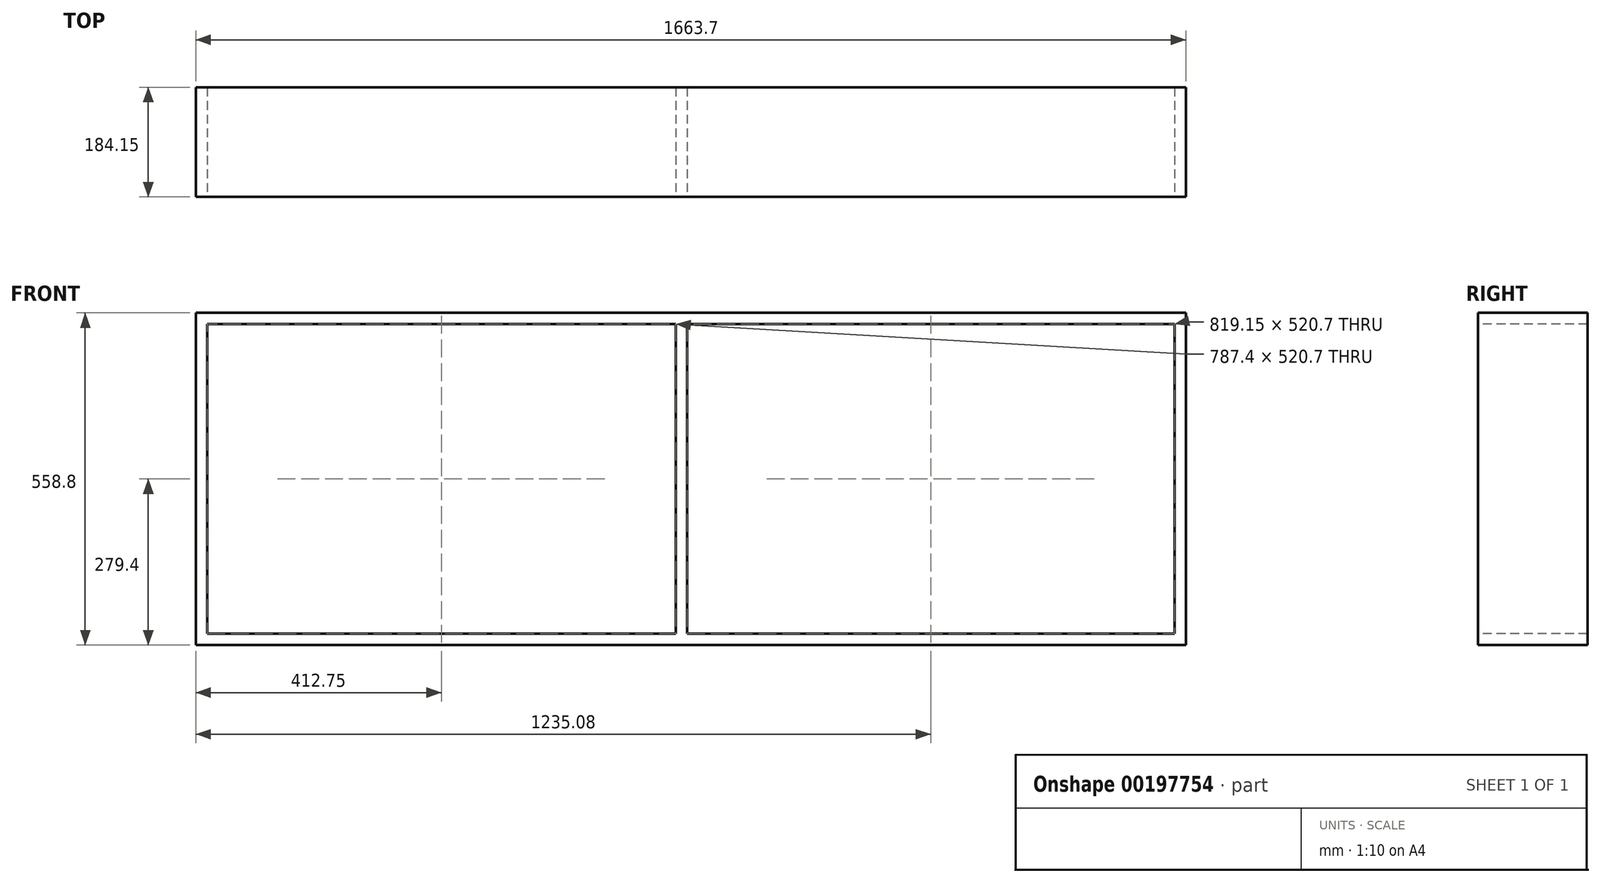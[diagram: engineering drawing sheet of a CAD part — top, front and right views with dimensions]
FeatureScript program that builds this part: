
annotation { "Feature Type Name" : "Feature", "Feature Type Description" : "" }
export const myFeature = defineFeature(function(context is Context, id is Id, definition is map)
    precondition{}
    {
        {
            var Q0;
            Q0=qCreatedBy(makeId("Front.planeOp"),FACE);
            var sketch = newSketch(context, id + "F0", { "sketchPlane" : qUnion([Q0])});
            skLineSegment(sketch, "E0.bottom", {"start": v(831.85, 279.4) * mm, "end": v(-831.85, 279.4) * mm});
            skLineSegment(sketch, "E0.top", {"start": v(831.85, -279.4) * mm, "end": v(-831.85, -279.4) * mm});
            skLineSegment(sketch, "E0.left", {"start": v(831.85, 279.4) * mm, "end": v(831.85, -279.4) * mm});
            skLineSegment(sketch, "E0.right", {"start": v(-831.85, 279.4) * mm, "end": v(-831.85, -279.4) * mm});
            skPoint(sketch, "E0.middle", {"position": v(0, 0) * mm});
            skLineSegment(sketch, "E1.bottom", {"start": v(-25.4, 260.35) * mm, "end": v(-812.8, 260.35) * mm});
            skLineSegment(sketch, "E1.top", {"start": v(-25.4, -260.35) * mm, "end": v(-812.8, -260.35) * mm});
            skLineSegment(sketch, "E1.left", {"start": v(-25.4, 260.35) * mm, "end": v(-25.4, -260.35) * mm});
            skLineSegment(sketch, "E1.right", {"start": v(-812.8, 260.35) * mm, "end": v(-812.8, -260.35) * mm});
            skPoint(sketch, "E1.middle", {"position": v(-419.1, 0) * mm});
            skLineSegment(sketch, "E2.bottom", {"start": v(812.8, 260.35) * mm, "end": v(-6.35, 260.35) * mm});
            skLineSegment(sketch, "E2.top", {"start": v(812.8, -260.35) * mm, "end": v(-6.35, -260.35) * mm});
            skLineSegment(sketch, "E2.left", {"start": v(812.8, 260.35) * mm, "end": v(812.8, -260.35) * mm});
            skLineSegment(sketch, "E2.right", {"start": v(-6.35, 260.35) * mm, "end": v(-6.35, -260.35) * mm});
            skPoint(sketch, "E2.middle", {"position": v(403.23, 0) * mm});
            skLineSegment(sketch, "E3.bottom", {"start": v(-209.55, -279.4) * mm, "end": v(831.85, -279.4) * mm});
            skLineSegment(sketch, "E3.top", {"start": v(-209.55, -730.25) * mm, "end": v(831.85, -730.25) * mm});
            skLineSegment(sketch, "E3.left", {"start": v(-209.55, -279.4) * mm, "end": v(-209.55, -730.25) * mm});
            skLineSegment(sketch, "E3.right", {"start": v(831.85, -279.4) * mm, "end": v(831.85, -730.25) * mm});
            skLineSegment(sketch, "E4.bottom", {"start": v(-831.85, -279.4) * mm, "end": v(-209.55, -279.4) * mm});
            skLineSegment(sketch, "E4.top", {"start": v(-831.85, -730.25) * mm, "end": v(-209.55, -730.25) * mm});
            skLineSegment(sketch, "E4.left", {"start": v(-831.85, -279.4) * mm, "end": v(-831.85, -730.25) * mm});
            skLineSegment(sketch, "E5.bottom", {"start": v(812.8, -298.45) * mm, "end": v(-190.5, -298.45) * mm});
            skLineSegment(sketch, "E5.top", {"start": v(812.8, -711.2) * mm, "end": v(-190.5, -711.2) * mm});
            skLineSegment(sketch, "E5.left", {"start": v(812.8, -298.45) * mm, "end": v(812.8, -711.2) * mm});
            skLineSegment(sketch, "E5.right", {"start": v(-190.5, -298.45) * mm, "end": v(-190.5, -711.2) * mm});
            skPoint(sketch, "E5.middle", {"position": v(311.15, -504.82) * mm});
            skLineSegment(sketch, "E6.bottom", {"start": v(-228.6, -298.45) * mm, "end": v(-812.8, -298.45) * mm});
            skLineSegment(sketch, "E6.top", {"start": v(-228.6, -495.3) * mm, "end": v(-812.8, -495.3) * mm});
            skLineSegment(sketch, "E6.left", {"start": v(-228.6, -298.45) * mm, "end": v(-228.6, -495.3) * mm});
            skLineSegment(sketch, "E6.right", {"start": v(-812.8, -298.45) * mm, "end": v(-812.8, -495.3) * mm});
            skPoint(sketch, "E6.middle", {"position": v(-520.7, -396.88) * mm});
            skLineSegment(sketch, "E7.bottom", {"start": v(-228.6, -514.35) * mm, "end": v(-812.8, -514.35) * mm});
            skLineSegment(sketch, "E7.top", {"start": v(-228.6, -711.2) * mm, "end": v(-812.8, -711.2) * mm});
            skLineSegment(sketch, "E7.left", {"start": v(-228.6, -514.35) * mm, "end": v(-228.6, -711.2) * mm});
            skLineSegment(sketch, "E7.right", {"start": v(-812.8, -514.35) * mm, "end": v(-812.8, -711.2) * mm});
            skPoint(sketch, "E7.middle", {"position": v(-520.7, -612.77) * mm});
            skSolve(sketch);
        }
        {
            var Q0;
            Q0=makeQuery(id+"F0.imprint","IMPRINT",FACE,{"disambiguationData":[TD([[makeQuery(id+"F0.imprint","IMPRINT",EDGE,{"derivedFrom":sQuery(id+"F0.wireOp",EDGE,"E0.bottom")}),1.0]])]});
            var Q1;
            Q1=makeQuery(id+"F0.imprint","IMPRINT",FACE,{"disambiguationData":[TD([[makeQuery(id+"F0.imprint","IMPRINT",EDGE,{"derivedFrom":sQuery(id+"F0.wireOp",EDGE,"E4.bottom")}),-1.0]])]});
            var Q2;
            Q2=makeQuery(id+"F0.imprint","IMPRINT",FACE,{"disambiguationData":[TD([[makeQuery(id+"F0.imprint","IMPRINT",EDGE,{"derivedFrom":sQuery(id+"F0.wireOp",EDGE,"E3.bottom")}),-1.0]])]});
            extrude(context, id + "F1", {"entities" : qUnion([Q0, Q1, Q2]), "oppositeDirection" : true, "depth" : 184.15 * mm});
        }
    });
